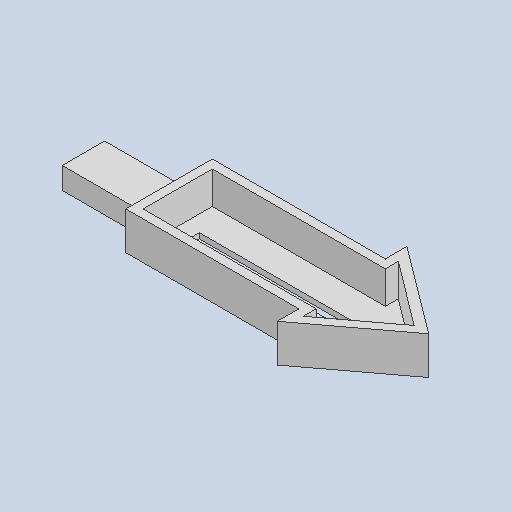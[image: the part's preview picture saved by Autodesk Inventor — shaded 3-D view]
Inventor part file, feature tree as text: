
AUTODESK INVENTOR PART (.ipt)
format: ipt  version: 2023 (Build 270158000, 158)  size: 123,904 bytes
history: native  units: in
note: dims shown in document units (in); Inventor stores cm internally (conversion verified against a paired STEP export)
features: sketch x5, other x3
ambient origin geometry x8: Origin, YZ Plane, XZ Plane, XY Plane, X Axis, Y Axis, Z Axis, Center Point
bodies: Solid1 (feature_tree)
feature tree (8):
  other  "Part_5_ledholder.ipt"
  other  "Solid1::Part_5_ledholder.ipt"
  other  "TaggingFeature1"
  sketch  "Sketch1"  dims[d0=0.3937in]
  sketch  "Sketch2"
  sketch  "Sketch3"
  sketch  "Sketch4"
  sketch  "Sketch6"
